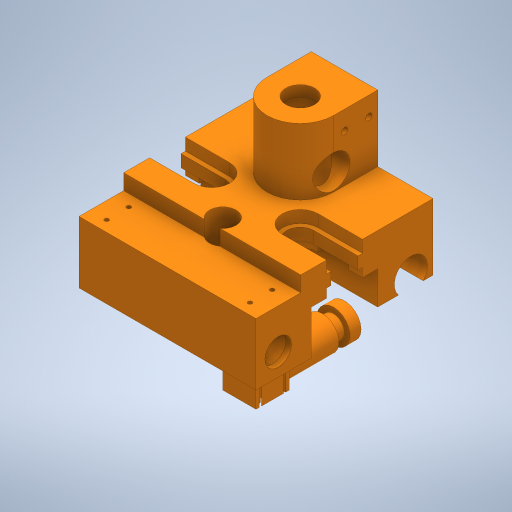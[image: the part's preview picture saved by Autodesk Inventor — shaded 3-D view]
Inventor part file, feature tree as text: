
AUTODESK INVENTOR PART (.ipt)
format: ipt  version: 2023 (Build 270158000, 158)  size: 674,816 bytes
history: native  units: mm
features: extrude x25, sketch x24, plane x3, mirror x2, other x1
ambient origin geometry x8: Origin, YZ Plane, XZ Plane, XY Plane, X Axis, Y Axis, Z Axis, Center Point
bodies: Solid1 (feature_tree)
feature tree (55):
  other  "<userpath>\OneDrive\ClawdDrive\Objet3D\3DPrinter\inventor\Parameters.xlsx"
  extrude  "Extrusion1"  Depth=80.0mm
  extrude  "Extrusion2"  Depth=40.0mm
  extrude  "Extrusion3"  Depth=20.0mm
  extrude  "Extrusion4"  Depth=16.2mm
  extrude  "Extrusion5"  Depth=4.0mm TaperAngle=0.0deg
  extrude  "Extrusion6"  Depth=4.0mm TaperAngle=0.0deg
  plane  "Work Plane1"
  mirror  "Mirror1"
  extrude  "Extrusion8"  Depth=8.1mm
  extrude  "Extrusion9"  Depth=25.0mm
  plane  "Work Plane2"
  mirror  "Mirror2"
  extrude  "Extrusion10"  Depth=15.0mm
  extrude  "Extrusion11"  Depth=15.0mm
  extrude  "Extrusion12"  Depth=5.0mm
  extrude  "Extrusion13"  Depth=80.0mm
  extrude  "Extrusion14"  Depth=15.0mm
  extrude  "Extrusion15"  Depth=10.0mm
  extrude  "Extrusion16"  Depth=20.2mm
  extrude  "Extrusion17"  TaperAngle=0.0deg  [1 undecoded]
  extrude  "Extrusion18"  Depth=1.9mm
  plane  "Work Plane3"
  extrude  "Extrusion19"  Depth=7.6mm
  extrude  "Extrusion20"  Depth=10.0mm
  extrude  "Extrusion21"  Depth=10.0mm
  extrude  "Extrusion22"  Depth=30.0mm
  extrude  "Extrusion23"  Depth=40.0mm
  extrude  "Extrusion24"  Depth=30.0mm TaperAngle=0.0deg
  extrude  "Extrusion25"  Depth=5.0mm TaperAngle=0.0deg
  extrude  "Extrusion26"  Depth=0.5mm TaperAngle=0.0deg
  sketch  "Sketch1"  dims[d0=80.0mm d1=80.0mm]
  sketch  "Sketch2"  dims[d2=15.0mm d3=0.0mm d7=40.0mm]
  sketch  "Sketch3"  dims[d8=20.0mm d9=12.2mm]
  sketch  "Sketch4"  dims[d10=10.0mm d11=0.0mm d12=16.2mm]
  sketch  "Sketch5"  dims[d13=4.0mm d14=0.0mm d15=5.5mm d16=0.0mm]
  sketch  "Sketch6"  dims[d17=13.8mm d18=4.0mm d19=0.0mm]
  sketch  "Sketch8"  dims[d20=16.2mm d21=8.1mm]
  sketch  "Sketch9"  dims[d22=25.0mm d23=25.0mm]
  sketch  "Sketch10"  dims[d24=15.0mm d25=15.0mm]
  sketch  "Sketch11"  dims[d29=15.0mm d32=15.0mm]
  sketch  "Sketch12"  dims[d33=5.0mm d34=5.0mm]
  sketch  "Sketch13"  dims[d35=80.0mm d36=0.0mm d37=0.0mm]
  sketch  "Sketch14"  dims[d38=15.0mm d39=15.0mm]
  sketch  "Sketch15"  dims[d40=60.0mm d41=10.0mm]
  sketch  "Sketch16"  dims[d42=10.0mm d49=20.2mm]
  sketch  "Sketch17"  dims[d50=7.0mm d51=0.0mm d52=0.0mm]
  sketch  "Sketch18"  dims[d53=1.9mm d54=1.9mm]
  sketch  "Sketch19"  dims[d55=7.6mm d56=7.6mm]
  sketch  "Sketch20"  dims[d57=10.0mm d58=4.9mm]
  sketch  "Sketch21"  dims[d59=10.0mm d60=0.0mm d61=12.0mm]
  sketch  "Sketch24"  dims[d62=20.0mm d63=0.0mm d64=30.0mm]
  sketch  "Sketch25"  dims[d65=20.0mm d66=40.0mm]
  sketch  "Sketch26"  dims[d67=20.0mm d68=30.0mm d69=0.0mm]
  sketch  "Sketch27"  dims[d70=13.0mm d71=5.0mm d72=0.0mm d73=35.0mm d74=0.0mm d75=2.9mm d76=2.9mm d77=11.0mm d78=4.0mm d79=8.5mm d80=8.5mm d81=15.0mm d82=0.0mm d83=6.0mm d84=15.0mm d85=8.0mm d86=17.0mm d87=0.0mm d88=15.0mm d89=0.0mm d90=32.5mm d91=15.0mm d92=15.0mm d93=32.5mm d94=45.0mm d95=0.0mm d96=7.5mm d97=7.5mm d98=15.0mm d99=32.5mm d100=0.0mm d101=-5.0mm d102=10.0mm d103=5.0mm d104=0.0mm d112=20.0mm d113=0.0mm d114=3.0mm d115=3.0mm d116=3.0mm d117=3.0mm d118=3.0mm d120=3.0mm d121=5.2mm d122=7.5mm d123=10.0mm d124=25.0mm d125=5.0mm d126=80.0mm d127=0.0mm d128=7.5mm d129=7.5mm d130=8.5mm d131=8.0mm d132=75.0mm d133=0.0mm d134=16.0mm d135=40.0mm d136=20.0mm d137=2.5mm d138=17.5mm d139=0.0mm d140=12.0mm d141=2.5mm d142=0.0mm d143=12.0mm d144=2.5mm d145=0.0mm d146=60.0mm d147=0.0mm d148=0.5mm d149=0.5mm]
note: 1 required parameter value undecoded (feature->parameter linkage not recoverable at this tier; creation-order binding heuristic only, values carry confidence <= 0.55)
